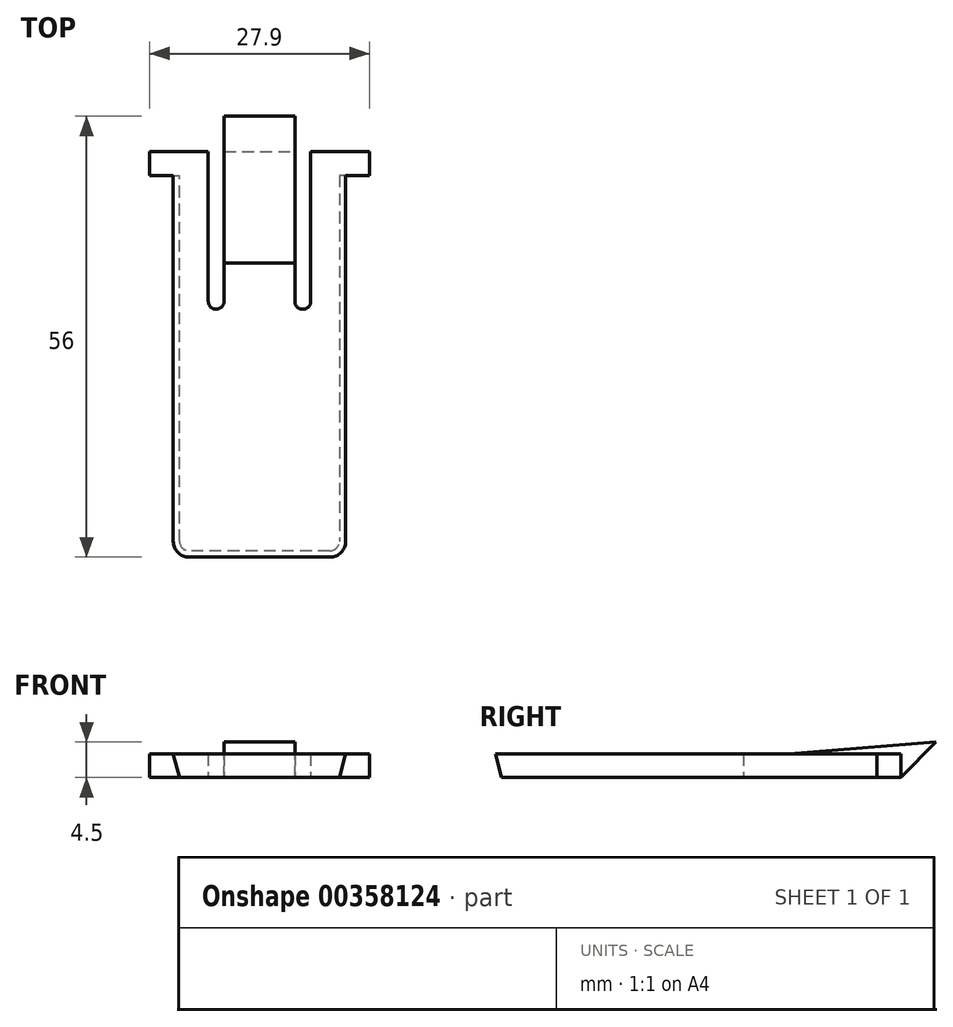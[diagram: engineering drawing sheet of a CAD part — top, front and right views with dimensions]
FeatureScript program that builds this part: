
annotation { "Feature Type Name" : "Feature", "Feature Type Description" : "" }
export const myFeature = defineFeature(function(context is Context, id is Id, definition is map)
    precondition{}
    {
        {
            var Q0;
            Q0=qCreatedBy(makeId("Top.planeOp"),FACE);
            var sketch = newSketch(context, id + "F0", { "sketchPlane" : qUnion([Q0])});
            skLineSegment(sketch, "E0.bottom", {"start": v(-10.95, 25.75) * mm, "end": v(-6.5, 25.75) * mm});
            skLineSegment(sketch, "E0.top", {"start": v(-8.95, -25.75) * mm, "end": v(8.95, -25.75) * mm});
            skLineSegment(sketch, "E0.left", {"start": v(-10.95, 25.75) * mm, "end": v(-10.95, -23.75) * mm});
            skLineSegment(sketch, "E0.right", {"start": v(10.95, 25.75) * mm, "end": v(10.95, -23.75) * mm});
            skLineSegment(sketch, "E1", {"start": v(-6.5, 25.75) * mm, "end": v(-6.5, 6.75) * mm});
            skLineSegment(sketch, "E2", {"start": v(-5.5, 5.75) * mm, "end": v(-5.5, 5.75) * mm});
            skLineSegment(sketch, "E3", {"start": v(-4.5, 6.75) * mm, "end": v(-4.5, 25.75) * mm});
            skLineSegment(sketch, "E4", {"start": v(4.5, 25.75) * mm, "end": v(4.5, 6.75) * mm});
            skLineSegment(sketch, "E5", {"start": v(5.5, 5.75) * mm, "end": v(5.5, 5.75) * mm});
            skLineSegment(sketch, "E6", {"start": v(6.5, 6.75) * mm, "end": v(6.5, 25.75) * mm});
            skLineSegment(sketch, "E7.trimOffspring", {"start": v(-4.5, 25.75) * mm, "end": v(4.5, 25.75) * mm});
            skLineSegment(sketch, "E8.trimOffspring", {"start": v(6.5, 25.75) * mm, "end": v(10.95, 25.75) * mm});
            skLineSegment(sketch, "E9", {"start": v(-10.95, 25.75) * mm, "end": v(-13.95, 25.75) * mm});
            skLineSegment(sketch, "E10", {"start": v(-13.95, 25.75) * mm, "end": v(-13.95, 22.75) * mm});
            skLineSegment(sketch, "E11", {"start": v(-13.95, 22.75) * mm, "end": v(-10.95, 22.75) * mm});
            skLineSegment(sketch, "E12", {"start": v(10.95, 25.75) * mm, "end": v(13.95, 25.75) * mm});
            skLineSegment(sketch, "E13", {"start": v(13.95, 25.75) * mm, "end": v(13.95, 22.75) * mm});
            skLineSegment(sketch, "E14", {"start": v(13.95, 22.75) * mm, "end": v(10.95, 22.75) * mm});
            skPoint(sketch, "E15.visualSharp", {"position": v(-10.95, -25.75) * mm});
            skArc(sketch, "E15.filletArc", {"start": v(-10.95, -23.75) * mm, "mid": v(-10.36, -25.16) * mm, "end": v(-8.95, -25.75) * mm});
            skPoint(sketch, "E16.visualSharp", {"position": v(10.95, -25.75) * mm});
            skArc(sketch, "E16.filletArc", {"start": v(8.95, -25.75) * mm, "mid": v(10.36, -25.16) * mm, "end": v(10.95, -23.75) * mm});
            skPoint(sketch, "E17.visualSharp", {"position": v(-6.5, 5.75) * mm});
            skArc(sketch, "E17.filletArc", {"start": v(-6.5, 6.75) * mm, "mid": v(-6.2, 6.04) * mm, "end": v(-5.5, 5.75) * mm});
            skPoint(sketch, "E18.visualSharp", {"position": v(-4.5, 5.75) * mm});
            skArc(sketch, "E18.filletArc", {"start": v(-5.5, 5.75) * mm, "mid": v(-4.8, 6.04) * mm, "end": v(-4.5, 6.75) * mm});
            skPoint(sketch, "E19.visualSharp", {"position": v(4.5, 5.75) * mm});
            skArc(sketch, "E19.filletArc", {"start": v(4.5, 6.75) * mm, "mid": v(4.8, 6.04) * mm, "end": v(5.5, 5.75) * mm});
            skPoint(sketch, "E20.visualSharp", {"position": v(6.5, 5.75) * mm});
            skArc(sketch, "E20.filletArc", {"start": v(5.5, 5.75) * mm, "mid": v(6.2, 6.04) * mm, "end": v(6.5, 6.75) * mm});
            skSolve(sketch);
        }
        {
            var Q0;
            Q0 = qSketchRegion(id + "F0", true);
            extrude(context, id + "F1", {"entities" : qUnion([Q0]), "depth" : 3 * mm});
        }
        {
            var Q0;
            Q0=qCreatedBy(makeId("Right.planeOp"),FACE);
            var sketch = newSketch(context, id + "F2", { "sketchPlane" : qUnion([Q0])});
            skLineSegment(sketch, "E21", {"start": v(25.75, 0) * mm, "end": v(30.25, 4.5) * mm});
            skLineSegment(sketch, "E22", {"start": v(30.25, 4.5) * mm, "end": v(-25.75, 0) * mm});
            skLineSegment(sketch, "E23", {"start": v(-25.75, 0) * mm, "end": v(25.75, 0) * mm});
            skSolve(sketch);
        }
        {
            var Q0;
            Q0 = qSketchRegion(id + "F2", true);
            extrude(context, id + "F3", {"entities" : qUnion([Q0]), "operationType" : NewBodyOperationType.ADD, "endBound" : BoundingType.SYMMETRIC, "depth" : 9 * mm});
        }
        {
            var Q0;
            Q0=makeQuery(id+"F1.opExtrude","CAP_EDGE",EDGE,{"disambiguationData":[OSD([sQuery(id+"F0.wireOp",EDGE,"E0.top")])],"isStart":true});
            chamfer(context, id + "F4", {"entities" : qUnion([Q0]), "chamferType" : ChamferType.OFFSET_ANGLE, "width" : 3 * mm, "oppositeDirection" : false, "angle" : 15 * degree, "tangentPropagation" : true});
        }
    });
